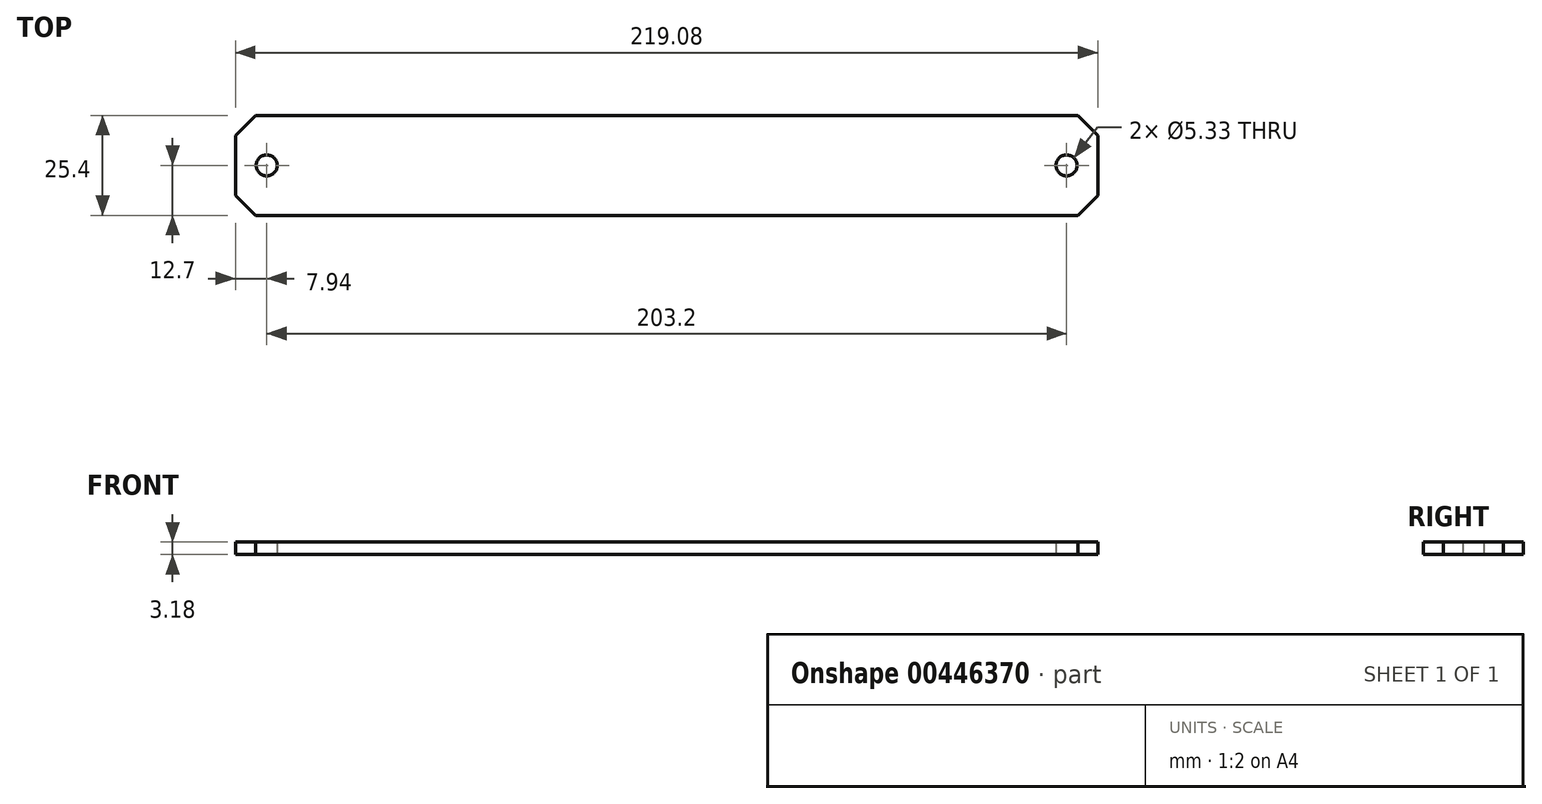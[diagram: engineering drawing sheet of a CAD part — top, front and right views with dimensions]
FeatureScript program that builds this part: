
annotation { "Feature Type Name" : "Feature", "Feature Type Description" : "" }
export const myFeature = defineFeature(function(context is Context, id is Id, definition is map)
    precondition{}
    {
        {
            var Q0;
            Q0=qCreatedBy(makeId("Top.planeOp"),FACE);
            var sketch = newSketch(context, id + "F0", { "sketchPlane" : qUnion([Q0])});
            skLineSegment(sketch, "E0.bottom", {"start": v(109.54, 12.7) * mm, "end": v(-109.54, 12.7) * mm});
            skLineSegment(sketch, "E0.top", {"start": v(109.54, -12.7) * mm, "end": v(-109.54, -12.7) * mm});
            skLineSegment(sketch, "E0.left", {"start": v(109.54, 12.7) * mm, "end": v(109.54, -12.7) * mm});
            skLineSegment(sketch, "E0.right", {"start": v(-109.54, 12.7) * mm, "end": v(-109.54, -12.7) * mm});
            skPoint(sketch, "E0.middle", {"position": v(0, 0) * mm});
            skLineSegment(sketch, "E1", {"start": v(-101.6, 12.7) * mm, "end": v(-101.6, -12.7) * mm, "construction": true});
            skCircle(sketch, "E2", {"center": v(-101.6, 0) * mm, "radius": 2.67 * mm});
            skCircle(sketch, "E3.MirrorC", {"center": v(101.6, 0) * mm, "radius": 2.67 * mm});
            skSolve(sketch);
        }
        {
            var Q0;
            Q0=makeQuery(id+"F0.imprint","IMPRINT",FACE,{"disambiguationData":[TD([[makeQuery(id+"F0.imprint","IMPRINT",EDGE,{"derivedFrom":sQuery(id+"F0.wireOp",EDGE,"E0.bottom")}),1.0]])]});
            extrude(context, id + "F1", {"entities" : qUnion([Q0]), "depth" : 3.17 * mm, "offsetDistance" : 25.4 * mm, "symmetric" : true});
        }
        {
            var Q0;
            Q0=makeQuery(id+"F1.opExtrude","SWEPT_EDGE",EDGE,{"disambiguationData":[OSD([sQuery(id+"F0.wireOp",EDGE,"E0.bottom"),sQuery(id+"F0.wireOp",EDGE,"E0.right")])]});
            var Q1;
            Q1=makeQuery(id+"F1.opExtrude","SWEPT_EDGE",EDGE,{"disambiguationData":[OSD([sQuery(id+"F0.wireOp",EDGE,"E0.top"),sQuery(id+"F0.wireOp",EDGE,"E0.right")])]});
            var Q2;
            Q2=makeQuery(id+"F1.opExtrude","SWEPT_EDGE",EDGE,{"disambiguationData":[OSD([sQuery(id+"F0.wireOp",EDGE,"E0.bottom"),sQuery(id+"F0.wireOp",EDGE,"E0.left")])]});
            var Q3;
            Q3=makeQuery(id+"F1.opExtrude","SWEPT_EDGE",EDGE,{"disambiguationData":[OSD([sQuery(id+"F0.wireOp",EDGE,"E0.top"),sQuery(id+"F0.wireOp",EDGE,"E0.left")])]});
            chamfer(context, id + "F2", {"entities" : qUnion([Q0, Q1, Q2, Q3]), "width" : 5.08 * mm, "tangentPropagation" : true});
        }
    });
